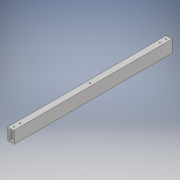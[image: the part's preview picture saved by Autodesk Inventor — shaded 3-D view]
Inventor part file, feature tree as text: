
AUTODESK INVENTOR PART (.ipt)
format: ipt  version: 2018 (Build 220112000, 112)  size: 120,832 bytes
history: native  units: in
note: dims shown in document units (in); Inventor stores cm internally (conversion verified against a paired STEP export)
features: extrude x2, sketch x2
ambient origin geometry x8: Origin, YZ Plane, XZ Plane, XY Plane, X Axis, Y Axis, Z Axis, Center Point
bodies: Solid1 (feature_tree)
feature tree (4):
  extrude  "Extrusion1"  Depth=2.0in
  extrude  "Extrusion2"  Depth=26.0in TaperAngle=0.0deg
  sketch  "Sketch1"  dims[d0=1.0in d1=2.0in]
  sketch  "Sketch2"  dims[d2=0.15in d3=26.0in d4=0.0in d5=0.5in d6=1.0in d7=0.5in d8=1.0in d9=0.2in d10=26.0in d11=0.0in]
